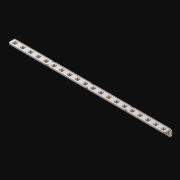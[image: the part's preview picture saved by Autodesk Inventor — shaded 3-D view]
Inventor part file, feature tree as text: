
AUTODESK INVENTOR PART (.ipt)
format: ipt  version: 2021 (Build 250183000, 183)  size: 718,336 bytes
history: native  units: in
note: dims shown in document units (in); Inventor stores cm internally (conversion verified against a paired STEP export)
features: extrude x41, other x40, sketch x3, pattern_linear x1, sheet_metal_op x1
ambient origin geometry x8: Origin, YZ Plane, XZ Plane, XY Plane, X Axis, Y Axis, Z Axis, Center Point
bodies: Solid1 (feature_tree)
feature tree (86):
  pattern_linear  "Rectangular Pattern1"  Spacing1=0.063in  [1 undecoded]
  extrude  "Extrusion1"  Depth=0.5in
  sketch  "Sketch1"  dims[d0=0.182in]
  other  "Srf1"
  sketch  "Sketch2"  dims[d1=0.063in d2=0.0in]
  other  "Srf2"
  other  "Srf3"
  other  "Srf5"
  other  "Srf7"
  other  "Srf9"
  other  "Srf11"
  other  "Srf13"
  other  "Srf15"
  other  "Srf17"
  other  "Srf19"
  other  "Srf21"
  other  "Srf23"
  other  "Srf25"
  other  "Srf27"
  other  "Srf29"
  other  "Srf31"
  other  "Srf33"
  other  "Srf35"
  other  "Srf37"
  other  "Srf39"
  other  "Srf4"
  other  "Srf6"
  other  "Srf8"
  other  "Srf10"
  other  "Srf12"
  other  "Srf14"
  other  "Srf16"
  other  "Srf18"
  other  "Srf20"
  other  "Srf22"
  other  "Srf24"
  other  "Srf26"
  other  "Srf28"
  other  "Srf30"
  other  "Srf32"
  other  "Srf34"
  other  "Srf36"
  other  "Srf38"
  other  "Srf40"
  sketch  "Sketch3"  dims[d3=0.182in d4=0.063in d5=0.0in d8=0.5in d9=7.5in d10=0.0in]
  sheet_metal_op  "Fold1"
  extrude  "ExtrusionSrf1"  Depth=7.5in TaperAngle=0.0deg
  extrude  "ExtrusionSrf2"  [1 undecoded]
  extrude  "ExtrusionSrf3"  [1 undecoded]
  extrude  "ExtrusionSrf4"  [1 undecoded]
  extrude  "ExtrusionSrf5"  [1 undecoded]
  extrude  "ExtrusionSrf6"  [1 undecoded]
  extrude  "ExtrusionSrf7"  [1 undecoded]
  extrude  "ExtrusionSrf8"  [1 undecoded]
  extrude  "ExtrusionSrf9"  [1 undecoded]
  extrude  "ExtrusionSrf10"  [1 undecoded]
  extrude  "ExtrusionSrf11"  [1 undecoded]
  extrude  "ExtrusionSrf12"  [1 undecoded]
  extrude  "ExtrusionSrf13"  [1 undecoded]
  extrude  "ExtrusionSrf14"  [1 undecoded]
  extrude  "ExtrusionSrf15"  [1 undecoded]
  extrude  "ExtrusionSrf16"  [1 undecoded]
  extrude  "ExtrusionSrf17"  [1 undecoded]
  extrude  "ExtrusionSrf18"  [1 undecoded]
  extrude  "ExtrusionSrf19"  [1 undecoded]
  extrude  "ExtrusionSrf20"  [1 undecoded]
  extrude  "ExtrusionSrf21"  [1 undecoded]
  extrude  "ExtrusionSrf37"  [1 undecoded]
  extrude  "ExtrusionSrf38"  [1 undecoded]
  extrude  "ExtrusionSrf39"  [1 undecoded]
  extrude  "ExtrusionSrf40"  [1 undecoded]
  extrude  "ExtrusionSrf41"  [1 undecoded]
  extrude  "ExtrusionSrf42"  [1 undecoded]
  extrude  "ExtrusionSrf43"  [1 undecoded]
  extrude  "ExtrusionSrf44"  [1 undecoded]
  extrude  "ExtrusionSrf45"  [1 undecoded]
  extrude  "ExtrusionSrf46"  [1 undecoded]
  extrude  "ExtrusionSrf47"  [1 undecoded]
  extrude  "ExtrusionSrf48"  [1 undecoded]
  extrude  "ExtrusionSrf49"  [1 undecoded]
  extrude  "ExtrusionSrf50"  [1 undecoded]
  extrude  "ExtrusionSrf51"  [1 undecoded]
  extrude  "ExtrusionSrf52"  [1 undecoded]
  extrude  "ExtrusionSrf53"  [1 undecoded]
  extrude  "ExtrusionSrf54"  [1 undecoded]
  extrude  "ExtrusionSrf55"  [1 undecoded]
note: 40 required parameter values undecoded (feature->parameter linkage not recoverable at this tier; creation-order binding heuristic only, values carry confidence <= 0.55)
